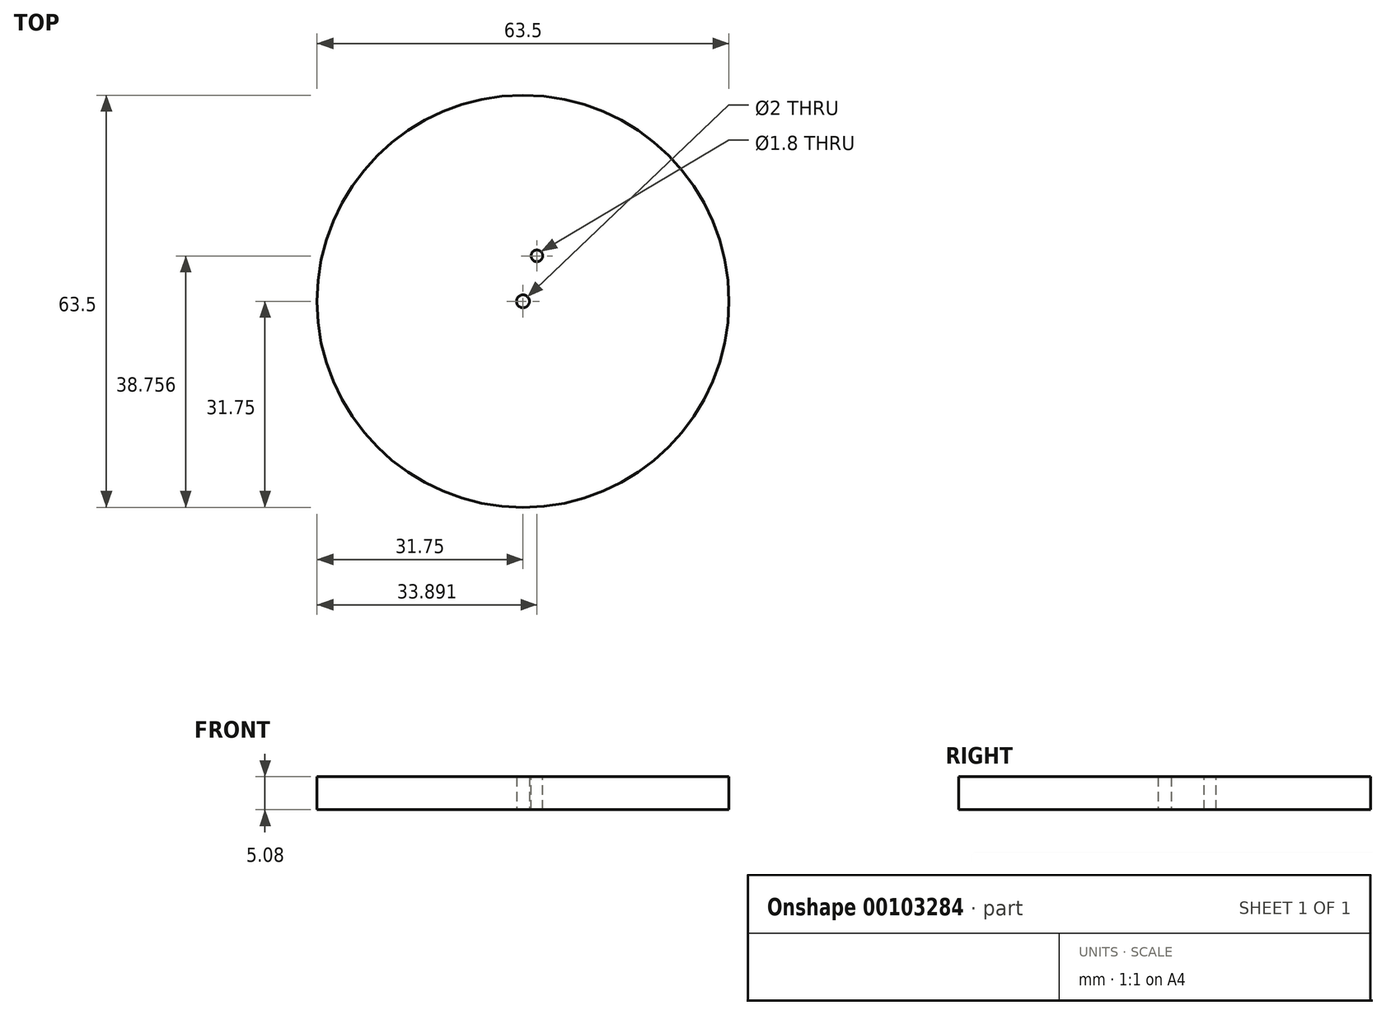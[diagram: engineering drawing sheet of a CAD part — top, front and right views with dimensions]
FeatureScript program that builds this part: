
annotation { "Feature Type Name" : "Feature", "Feature Type Description" : "" }
export const myFeature = defineFeature(function(context is Context, id is Id, definition is map)
    precondition{}
    {
        {
            var Q0;
            Q0=qCreatedBy(makeId("Top.planeOp"),FACE);
            var sketch = newSketch(context, id + "F0", { "sketchPlane" : qUnion([Q0])});
            skCircle(sketch, "E0", {"center": v(0, 0) * mm, "radius": 31.75 * mm});
            skSolve(sketch);
        }
        {
            var Q0;
            Q0=makeQuery(id+"F0.imprint","IMPRINT",FACE,{"disambiguationData":[TD([[makeQuery(id+"F0.imprint","IMPRINT",EDGE,{"derivedFrom":sQuery(id+"F0.wireOp",EDGE,"E0")}),1.0]])]});
            extrude(context, id + "F1", {"entities" : qUnion([Q0]), "depth" : 5.08 * mm});
        }
        {
            var Q0;
            Q0=makeQuery(id+"F1.opExtrude","CAP_FACE",FACE,{"disambiguationData":[OSD([sQuery(id+"F0.wireOp",EDGE,"E0")])],"isStart":true});
            var sketch = newSketch(context, id + "F2", { "sketchPlane" : qUnion([Q0])});
            skCircle(sketch, "E1", {"center": v(0, 0) * mm, "radius": 1 * mm});
            skSolve(sketch);
        }
        {
            var Q0;
            Q0=makeQuery(id+"F2.imprint","IMPRINT",FACE,{"disambiguationData":[TD([[makeQuery(id+"F2.imprint","IMPRINT",EDGE,{"derivedFrom":sQuery(id+"F2.wireOp",EDGE,"E1")}),1.0]])]});
            extrude(context, id + "F3", {"entities" : qUnion([Q0]), "operationType" : NewBodyOperationType.REMOVE, "endBound" : BoundingType.THROUGH_ALL, "oppositeDirection" : true, "depth" : 25.4 * mm});
        }
        {
            var Q0;
            Q0=makeQuery(id+"F1.opExtrude","CAP_FACE",FACE,{"disambiguationData":[OSD([sQuery(id+"F0.wireOp",EDGE,"E0")])],"isStart":false});
            var sketch = newSketch(context, id + "F4", { "sketchPlane" : qUnion([Q0])});
            skPoint(sketch, "E2", {"position": v(2.14, 7) * mm});
            skCircle(sketch, "E3", {"center": v(2.14, 7) * mm, "radius": 0.9 * mm});
            skSolve(sketch);
        }
        {
            var Q0;
            Q0=makeQuery(id+"F4.imprint","IMPRINT",FACE,{"disambiguationData":[TD([[makeQuery(id+"F4.imprint","IMPRINT",EDGE,{"derivedFrom":sQuery(id+"F4.wireOp",EDGE,"E3")}),1.0]])]});
            extrude(context, id + "F5", {"entities" : qUnion([Q0]), "operationType" : NewBodyOperationType.REMOVE, "endBound" : BoundingType.THROUGH_ALL, "oppositeDirection" : true, "depth" : 25.4 * mm});
        }
    });
